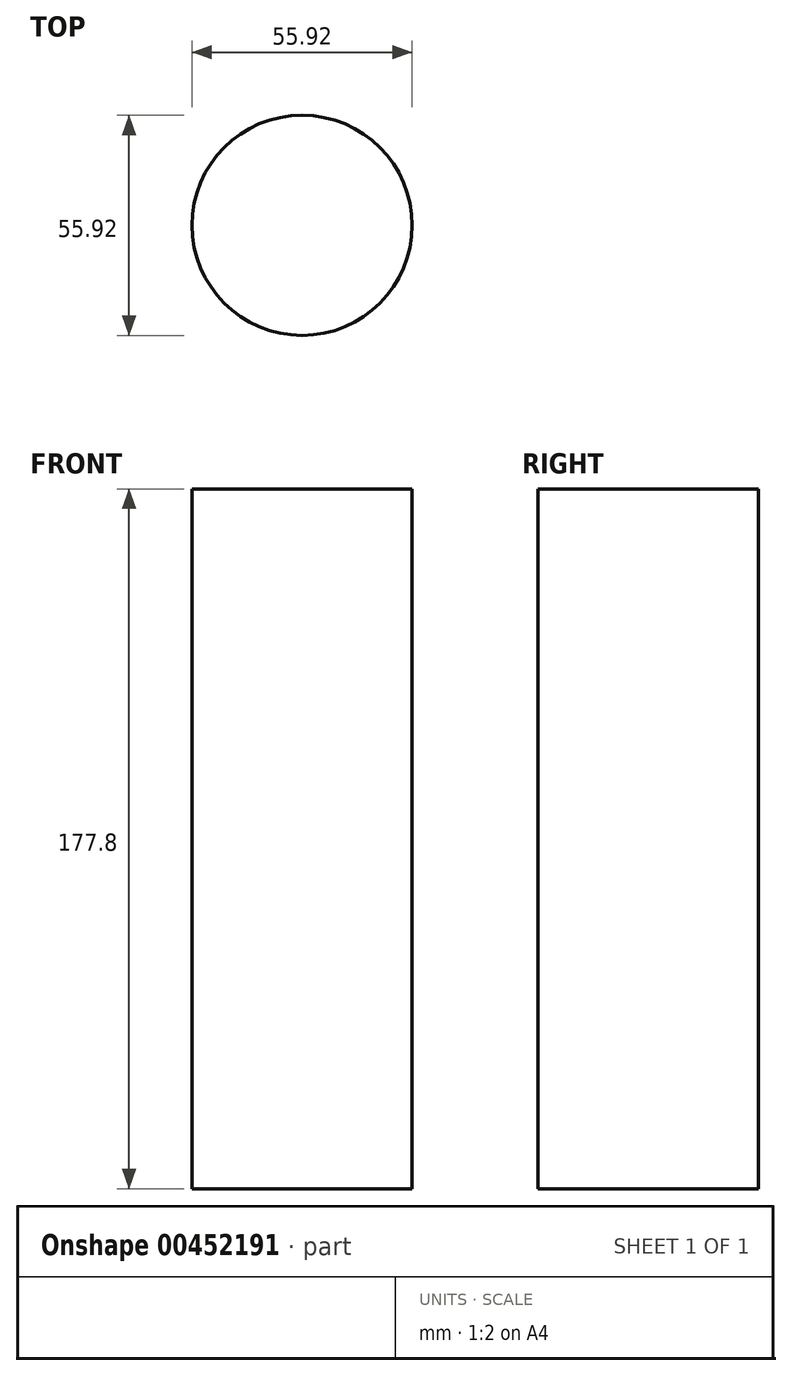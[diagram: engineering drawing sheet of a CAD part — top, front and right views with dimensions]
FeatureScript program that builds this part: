
annotation { "Feature Type Name" : "Feature", "Feature Type Description" : "" }
export const myFeature = defineFeature(function(context is Context, id is Id, definition is map)
    precondition{}
    {
        {
            var Q0;
            Q0=qCreatedBy(makeId("Top.planeOp"),FACE);
            var sketch = newSketch(context, id + "F0", { "sketchPlane" : qUnion([Q0])});
            skCircle(sketch, "E0", {"center": v(0, 0) * mm, "radius": 27.96 * mm});
            skSolve(sketch);
        }
        {
            var Q0;
            Q0=makeQuery(id+"F0.imprint","IMPRINT",FACE,{"disambiguationData":[TD([[makeQuery(id+"F0.imprint","IMPRINT",EDGE,{"derivedFrom":sQuery(id+"F0.wireOp",EDGE,"E0")}),1.0]])]});
            var Q1;
            Q1=sQuery(id+"F0.wireOp",EDGE,"E0");
            extrude(context, id + "F1", {"entities" : qUnion([Q0]), "surfaceEntities" : qUnion([Q1]), "depth" : 177.8 * mm});
        }
    });
